# Revit family: Sanitary_Showers_hansgrohe_58154XXX-Flexaplus-Complete-set-basic-set-and-finish-set-waste-and-overflow-set-for-bathtubs_NEW
name_source: partatom
category: Plumbing Fixtures
units: mm (PartAtom-declared; Revit-internal decimal feet)

## family parameters
Cut with Voids When Loaded = Yes
Host = Face
Maintain Annotation Orientation = No
OmniClass Number = 23.31.15.17.23
OmniClass Title = Bathtub Drains
Part Type = Normal
Room Calculation Point = No
Round Connector Dimension = Use Diameter
Shared = No

## types (1)
- 58154XXX Flexaplus Complete set basic set and finish set waste and overflow set for bathtubs
    Connector Description = Water Outlet 50 mm
    Default Elevation = 1219 mm
    Description = Flexaplus Complete set basic set and finish set waste and overflow set for bathtubs
    Diameter = 50 mm
    Inlet Connector Description = Water Inlet 12.7mm
    Inlet Diameter = 13 mm  [stored 0.0426509 ft]
    Manufacturer = Hansgrohe
    Material 1 = Hansgrohe - Metal - Chrome
    Material 2 = Hansgrohe - Plastic - Black
    Material 3 = Hansgrohe - Metal - Brass
    Material 4 = Hansgrohe - Plastic - Grey
    Model = 58154XXX
    Product Page URL = https://www.hansgrohe.com
    Product data url = https://bimobject.com
    URL = https://www.hansgrohe.com
    Version = 1

note: [stored X ft] marks values corroborated as IEEE doubles in the binary element streams (Revit-internal decimal feet)

## geometry (parser evidence)
native form markers: Sweep x2
no freeform markers — native parametric forms only
